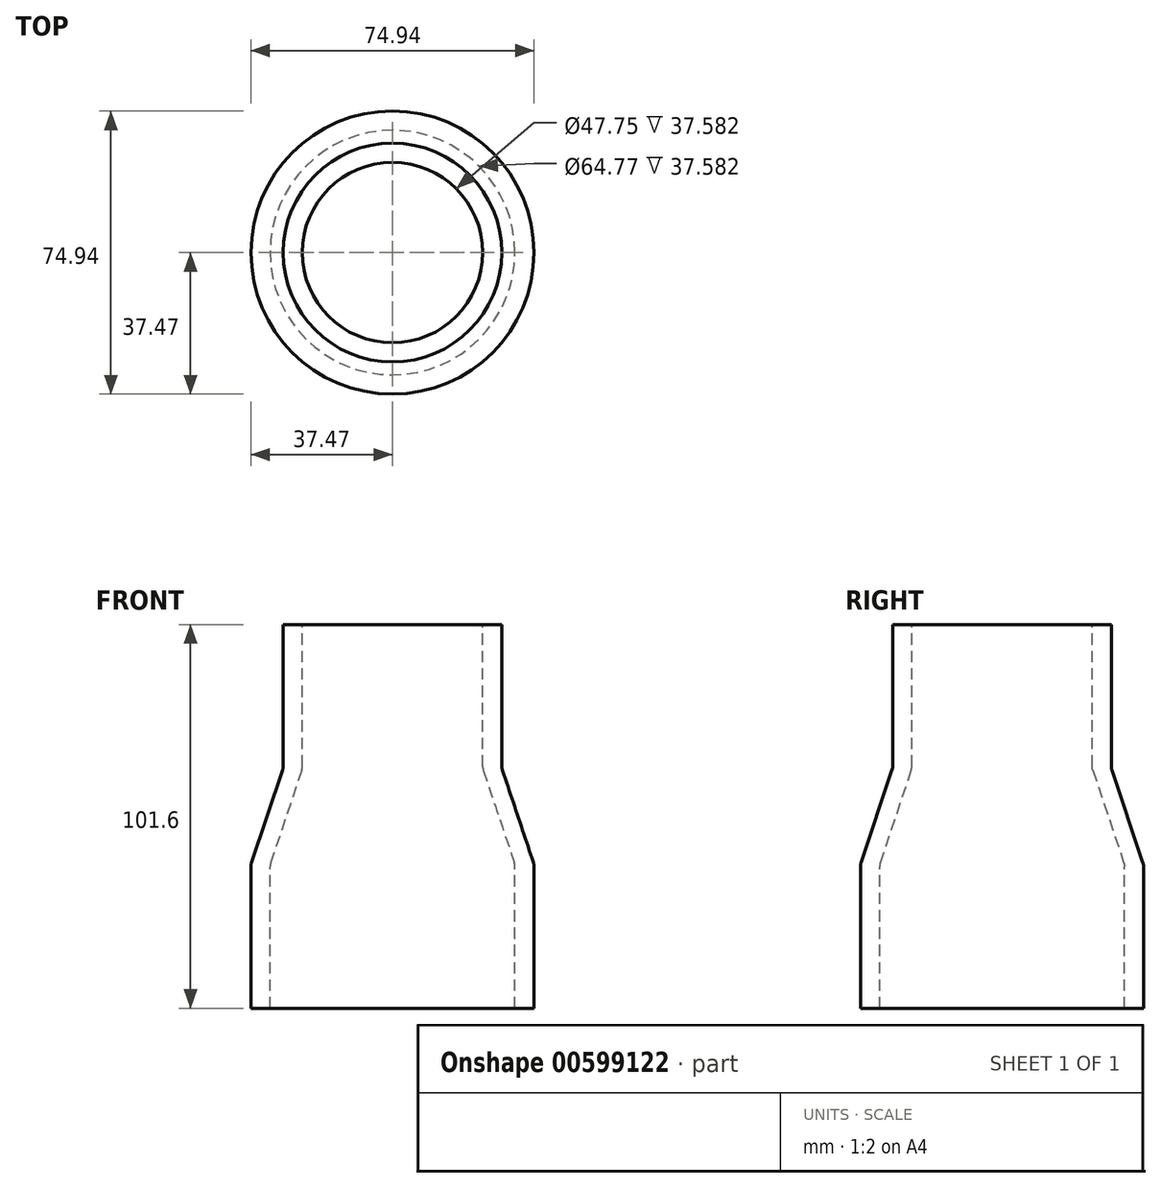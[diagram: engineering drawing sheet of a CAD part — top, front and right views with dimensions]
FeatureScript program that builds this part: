
annotation { "Feature Type Name" : "Feature", "Feature Type Description" : "" }
export const myFeature = defineFeature(function(context is Context, id is Id, definition is map)
    precondition{}
    {
        {
            var Q0;
            Q0=qCreatedBy(makeId("Front.planeOp"),FACE);
            var sketch = newSketch(context, id + "F0", { "sketchPlane" : qUnion([Q0])});
            skLineSegment(sketch, "E0", {"start": v(0, 114.3) * mm, "end": v(0, -114.3) * mm, "construction": true});
            skLineSegment(sketch, "E1", {"start": v(-83.03, 0) * mm, "end": v(83.03, 0) * mm, "construction": true});
            skLineSegment(sketch, "E2.bottom", {"start": v(23.88, 50.8) * mm, "end": v(28.96, 50.8) * mm});
            skLineSegment(sketch, "E2.top", {"start": v(23.88, 12.7) * mm, "end": v(28.96, 12.7) * mm});
            skLineSegment(sketch, "E2.left", {"start": v(23.88, 50.8) * mm, "end": v(23.88, 13.22) * mm});
            skLineSegment(sketch, "E2.right", {"start": v(28.96, 50.8) * mm, "end": v(28.96, 13.22) * mm});
            skLineSegment(sketch, "E3.bottom", {"start": v(32.38, -12.7) * mm, "end": v(37.46, -12.7) * mm});
            skLineSegment(sketch, "E3.top", {"start": v(32.38, -50.8) * mm, "end": v(37.46, -50.8) * mm});
            skLineSegment(sketch, "E3.left", {"start": v(32.38, -13.22) * mm, "end": v(32.38, -50.8) * mm});
            skLineSegment(sketch, "E3.right", {"start": v(37.46, -13.22) * mm, "end": v(37.46, -50.8) * mm});
            skLineSegment(sketch, "E4", {"start": v(24.04, 12.2) * mm, "end": v(32.22, -12.2) * mm});
            skLineSegment(sketch, "E5", {"start": v(29.12, 12.2) * mm, "end": v(37.3, -12.2) * mm});
            skPoint(sketch, "E6.visualSharp", {"position": v(28.96, 12.7) * mm});
            skArc(sketch, "E6.filletArc", {"start": v(28.96, 13.22) * mm, "mid": v(29, 12.7) * mm, "end": v(29.12, 12.2) * mm});
            skPoint(sketch, "E7.visualSharp", {"position": v(37.46, -12.7) * mm});
            skArc(sketch, "E7.filletArc", {"start": v(37.46, -13.22) * mm, "mid": v(37.42, -12.7) * mm, "end": v(37.3, -12.2) * mm});
            skPoint(sketch, "E8.visualSharp", {"position": v(32.38, -12.7) * mm});
            skArc(sketch, "E8.filletArc", {"start": v(32.38, -13.22) * mm, "mid": v(32.34, -12.7) * mm, "end": v(32.22, -12.2) * mm});
            skPoint(sketch, "E9.visualSharp", {"position": v(23.88, 12.7) * mm});
            skArc(sketch, "E9.filletArc", {"start": v(23.88, 13.22) * mm, "mid": v(23.92, 12.7) * mm, "end": v(24.04, 12.2) * mm});
            skSolve(sketch);
        }
        {
            var Q0;
            Q0=makeQuery(id+"F0.imprint","IMPRINT",FACE,{"disambiguationData":[TD([[makeQuery(id+"F0.imprint","IMPRINT",EDGE,{"derivedFrom":sQuery(id+"F0.wireOp",EDGE,"E2.bottom")}),-1.0]])]});
            var Q1;
            Q1=sQuery(id+"F0.wireOp",EDGE,"E0");
            revolve(context, id + "F1", {"entities" : qUnion([Q0]), "axis" : qUnion([Q1]), "revolveType" : RevolveType.FULL});
        }
    });
